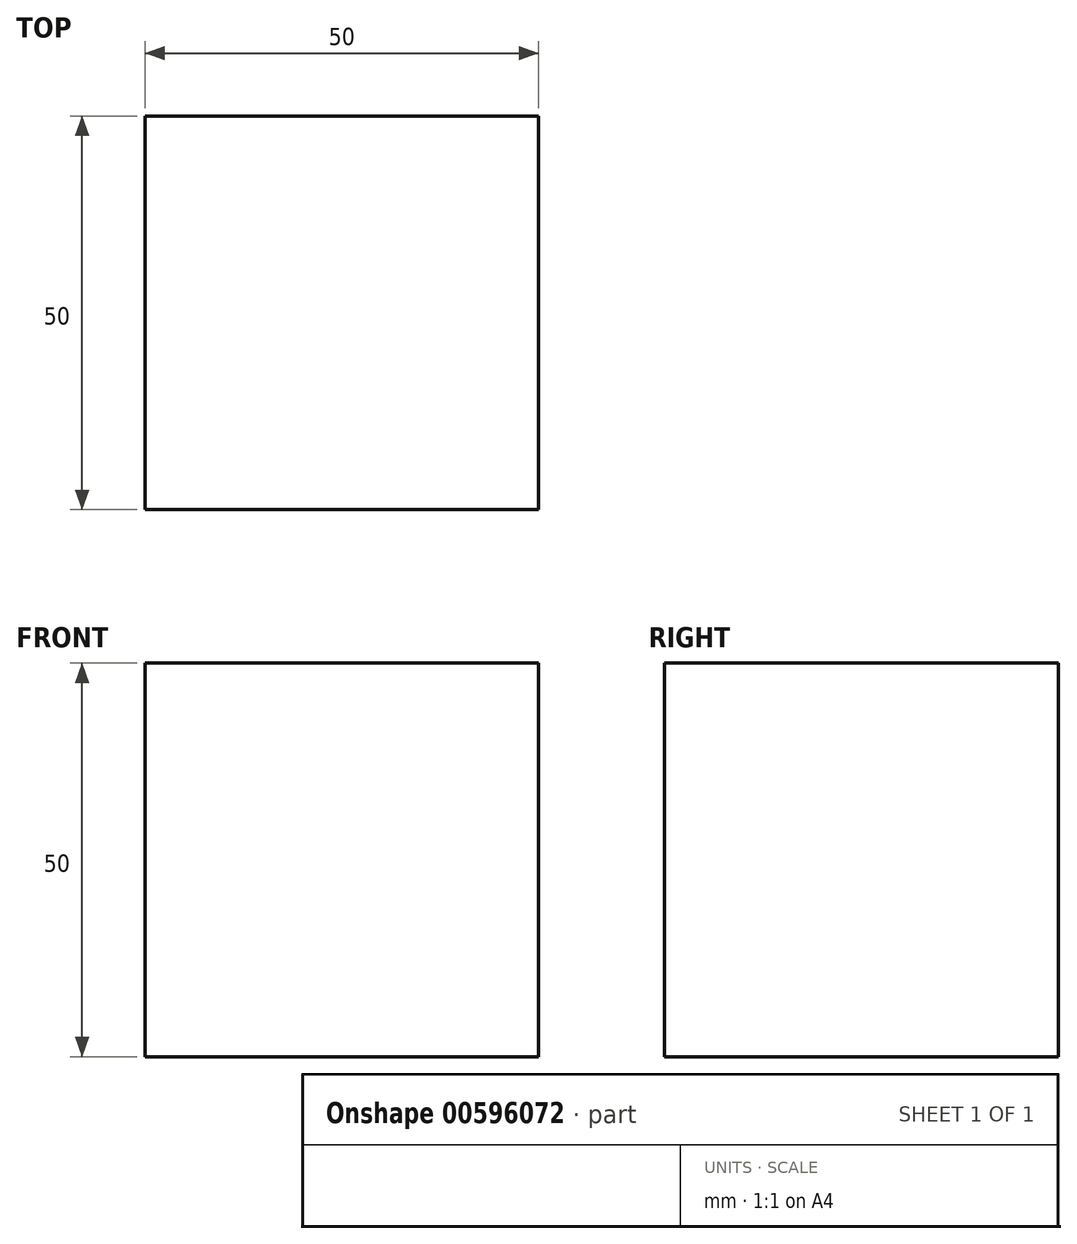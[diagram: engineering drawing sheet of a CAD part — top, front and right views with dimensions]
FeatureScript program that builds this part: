
annotation { "Feature Type Name" : "Feature", "Feature Type Description" : "" }
export const myFeature = defineFeature(function(context is Context, id is Id, definition is map)
    precondition{}
    {
        {
            var Q0;
            Q0=qCreatedBy(makeId("Top.planeOp"),FACE);
            var sketch = newSketch(context, id + "F0", { "sketchPlane" : qUnion([Q0])});
            skLineSegment(sketch, "E0.bottom", {"start": v(-25, -25) * mm, "end": v(25, -25) * mm});
            skLineSegment(sketch, "E0.top", {"start": v(-25, 25) * mm, "end": v(25, 25) * mm});
            skLineSegment(sketch, "E0.left", {"start": v(-25, -25) * mm, "end": v(-25, 25) * mm});
            skLineSegment(sketch, "E0.right", {"start": v(25, -25) * mm, "end": v(25, 25) * mm});
            skPoint(sketch, "E0.middle", {"position": v(0, 0) * mm});
            skSolve(sketch);
        }
        {
            var Q0;
            Q0 = qSketchRegion(id + "F0", true);
            extrude(context, id + "F1", {"entities" : qUnion([Q0]), "depth" : 50 * mm, "offsetDistance" : 25 * mm});
        }
    });
